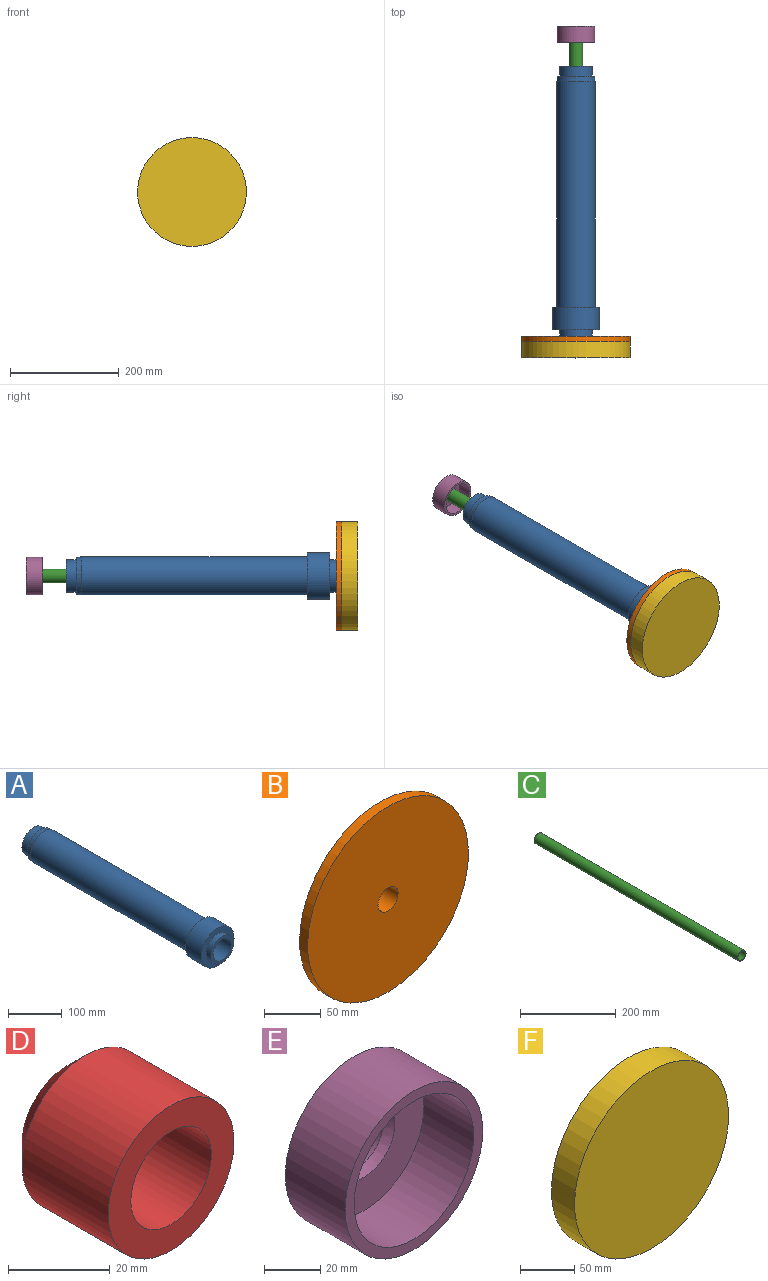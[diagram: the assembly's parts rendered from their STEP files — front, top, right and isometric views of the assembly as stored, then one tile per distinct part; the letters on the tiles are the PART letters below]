
ASSEMBLY  parts=6 mates=5
PART A: 15 faces, bbox 86x496x86 mm
  f0: cylinder r=30mm len=60mm, axis (0,-1,0), area 2261.9mm2, adj f1,f4
  f1: plane 60x60mm, normal (0,-1,0), area 1092.5mm2, adj f0,f12
  f2: cylinder r=43mm len=86mm, axis (0,-1,0), area 11077.3mm2, adj f3,f4
  f3: plane 86x86mm, normal (0,1,0), area 1944.5mm2, adj f2,f5
  f4: plane 86x86mm, normal (0,-1,0), area 2981.4mm2, adj f0,f2
  f5: cylinder r=35.07mm len=415mm, axis (0,-1,0), area 91451mm2, adj f3,f6
  f6: cone r=35.07mm half-angle=5deg, axis (0,-1,0), area 2184.5mm2, adj f5,f7
  f7: plane 68.39x68.39mm, normal (0,1,0), area 846.5mm2, adj f6,f8
  f8: cylinder r=30mm len=60mm, axis (0,-1,0), area 3392.9mm2, adj f7,f9
  f9: plane 60x60mm, normal (0,1,0), area 1092.5mm2, adj f8,f10
  f10: cylinder r=23.5mm len=47mm, axis (0,1,0), area 4282mm2, adj f9,f11
  f11: plane 47x47mm, normal (0,1,0), area 282.7mm2, adj f10,f14
  f12: cylinder r=23.5mm len=47mm, axis (0,-1,0), area 5315.6mm2, adj f1,f13
  f13: plane 47x47mm, normal (0,-1,0), area 282.7mm2, adj f12,f14
  f14: cylinder r=21.5mm len=431mm, axis (0,-1,0), area 58223.1mm2, adj f11,f13
PART B: 8 faces, bbox 200x50x200 mm
  f0: cylinder r=100mm len=200mm, axis (0,-1,0), area 6283.2mm2, adj f2,f3
  f1: cylinder r=12.5mm len=50mm, axis (0,-1,0), area 3927mm2, adj f3,f5
  f2: plane 200x200mm, normal (0,1,0), area 29606.4mm2, adj f0,f6
  f3: plane 200x200mm, normal (0,-1,0), area 30925.1mm2, adj f0,f1
  f4: cylinder r=17.5mm len=37mm, axis (0,-1,0), area 4068.4mm2, adj f5,f7
  f5: cone r=12.5mm half-angle=45deg, axis (0,-1,0), area 666.4mm2, adj f1,f4
  f6: cylinder r=24mm len=48mm, axis (0,1,0), area 301.6mm2, adj f2,f7
  f7: plane 48x48mm, normal (0,1,0), area 847.4mm2, adj f4,f6
PART C: 4 faces, bbox 25x600x25 mm
  f0: cylinder r=11.2mm len=600mm, axis (0,-1,0), area 42223mm2, adj f2,f3
  f1: cylinder r=12.5mm len=600mm, axis (0,-1,0), area 47123.9mm2, adj f2,f3
  f2: plane 25x25mm, normal (0,1,0), area 96.8mm2, adj f0,f1
  f3: plane 25x25mm, normal (0,-1,0), area 96.8mm2, adj f0,f1
PART D: 5 faces, bbox 35x29x35 mm
  f0: cylinder r=11.2mm len=29mm, axis (0,1,0), area 2040.8mm2, adj f2,f3
  f1: cylinder r=17.5mm len=35mm, axis (0,1,0), area 2638.9mm2, adj f2,f4
  f2: plane 35x35mm, normal (0,-1,0), area 568mm2, adj f0,f1
  f3: plane 25x25mm, normal (0,1,0), area 96.8mm2, adj f0,f4
  f4: cone r=12.5mm half-angle=45deg, axis (0,-1,0), area 666.4mm2, adj f1,f3
PART E: 7 faces, bbox 69x30x69 mm
  f0: cylinder r=34.5mm len=69mm, axis (0,-1,0), area 6503.1mm2, adj f1,f2
  f1: plane 69x69mm, normal (0,1,0), area 3248.4mm2, adj f0,f5
  f2: plane 69x69mm, normal (0,-1,0), area 911.8mm2, adj f0,f3
  f3: cylinder r=30mm len=60mm, axis (0,-1,0), area 4712.4mm2, adj f2,f4
  f4: plane 60x60mm, normal (0,-1,0), area 2072.7mm2, adj f3,f6
  f5: cylinder r=12.5mm len=25mm, axis (0,-1,0), area 157.1mm2, adj f1,f6
  f6: cone r=12.5mm half-angle=45deg, axis (0,-1,0), area 373.2mm2, adj f4,f5
PART F: 6 faces, bbox 200x30x200 mm
  f0: cylinder r=100mm len=200mm, axis (0,1,0), area 18798.4mm2, adj f1,f2,f3
  f1: plane 200x200mm, normal (0,-1,0), area 31415.9mm2, adj f0
  f2: plane 200x200mm, normal (0,1,0), area 30925.1mm2, adj f0,f4
  f3: cylinder r=4mm len=88.16mm, axis (1,0,0), area 2206.3mm2, adj f0,f4
  f4: cylinder r=12.5mm len=25mm, axis (0,1,0), area 1912.6mm2, adj f2,f3,f5
  f5: plane 25x25mm, normal (0,1,0), area 490.9mm2, adj f4
PLACE A t=(-19.96,-276.32,62.95)mm
PLACE B t=(-19.96,-276.32,62.95)mm
PLACE C t=(-19.96,-276.32,62.95)mm
PLACE D t=(-19.96,-394.32,62.95)mm
PLACE E t=(-19.96,-231.32,62.95)mm
PLACE F t=(-19.96,-276.32,62.95)mm
MATE fastened B.f1 <-> F.f4  axis (0,-1,0) through (-19.96,-276.32,62.95)mm
MATE revolute E.f5 <-> C.f1  axis (0,1,0) through (-19.96,303.68,62.95)mm
MATE fastened A.f10 <-> B.f6  axis (0,-1,0) through (-19.96,-266.32,62.95)mm
MATE fastened C.f1 <-> F.f4  axis (0,-1,0) through (-19.96,-296.32,62.95)mm
MATE slider D.f0 <-> C.f1  axis (0,-1,0) through (-19.96,81.68,62.95)mm
